# Revit family: SQN-HP
name_source: partatom
category: Mechanical Equipment
units: mm (PartAtom-declared; Revit-internal decimal feet)

## family parameters
Always vertical = Yes
Cut with Voids When Loaded = No
Part Type = Normal
Room Calculation Point = No
Round Connector Dimension = Use Diameter
Shared = No
Work Plane-Based = No

## types (13) — shared parameters
1.5 = 0' - 1 1/2"
HALF_F = 0' - 11 1/32"
HALF_G = 0' - 11 13/32"
Manufacturer = Loren Cook Company
Model = SQN-HP
ONE EIGTH = 0' - 0 1/8"
T_SQ = 1' - 0"
T_SQ_HALF = 0' - 6"
Type Comments = Centrifugal Square Inline High Pressure Belt Drive
URL = www.lorencook.com
ZERO = 0' - 0"

## per-type parameters (varying)
- 135_SQN-HP: A_SUB=1' - 6"; B_SUB=1' - 8 1/4"; B_SUB_MIN_.125=1' - 8 1/8"; C_SUB=1' - 10 1/4"; DEPTH=1' - 8 1/4"; D_PLUS_2=1' - 10 3/4"; D_SUB=1' - 8 3/4"; D_SUB_MINUS_.25=1' - 8 1/2"; D_SUB_TENTH=0' - 2 1/16"; E_SUB=1' - 0 1/2"; E_SUB_DIRECT=1' - 10 3/4"; FLANGE=0' - 1"; FOURTH_B=0' - 5 1/16"; F_SUB=1' - 1 1/8"; G_SUB=1' - 2 1/4"; HALFC-B=0' - 1"; HALF_2H+D=0' - 11 3/8"; HALF_B=0' - 10 1/8"; HALF_B-G=0' - 3"; HALF_D=0' - 10 3/8"; HALF_D-A=0' - 1 3/8"; HALF_D-F=0' - 3 13/16"; HALF_D_SUB=0' - 10 3/8"; HALF_D_SUB_MIN_.25=0' - 10 1/4"; HALF_MP=0' - 3 17/32"; INLET_RADIUS=0' - 5 3/16"; IN_RAD-D_SUB_TENTH=0' - 3 1/8"; IN_TENTH=0' - 3 1/8"; MOTOR_DEPTH=-0' - 11 7/8"; NEGHALFC-B=-0' - 1"; NEG_HALF2H+D=-0' - 11 3/8"; NEG_HALF_D=-0' - 10 3/8"; RAIL_SPACING=0' - 10 1/8"; SHAFT_RAD=0' - 1 1/32"; TENTHB+FOURTHB=-0' - 7 3/32"; TENTH_B=-0' - 2 1/32"
- 150_SQN-HP: A_SUB=1' - 8"; B_SUB=1' - 9 7/8"; B_SUB_MIN_.125=1' - 9 3/4"; C_SUB=1' - 11 7/8"; DEPTH=1' - 9 7/8"; D_PLUS_2=2' - 1"; D_SUB=1' - 11"; D_SUB_MINUS_.25=1' - 10 3/4"; D_SUB_TENTH=0' - 2 5/16"; E_SUB=1' - 0 3/4"; E_SUB_DIRECT=2' - 1"; FLANGE=0' - 1"; FOURTH_B=0' - 5 15/32"; F_SUB=1' - 4 1/8"; G_SUB=1' - 3 15/16"; HALFC-B=0' - 1"; HALF_2H+D=1' - 0 1/2"; HALF_B=0' - 10 15/16"; HALF_B-G=0' - 2 31/32"; HALF_D=0' - 11 1/2"; HALF_D-A=0' - 1 1/2"; HALF_D-F=0' - 3 7/16"; HALF_D_SUB=0' - 11 1/2"; HALF_D_SUB_MIN_.25=0' - 11 3/8"; HALF_MP=0' - 3 27/32"; INLET_RADIUS=0' - 5 3/4"; IN_RAD-D_SUB_TENTH=0' - 3 7/16"; IN_TENTH=0' - 3 7/16"; MOTOR_DEPTH=-1' - 0 11/16"; NEGHALFC-B=-0' - 1"; NEG_HALF2H+D=-1' - 0 1/2"; NEG_HALF_D=-0' - 11 1/2"; RAIL_SPACING=0' - 10 15/16"; SHAFT_RAD=0' - 1 1/16"; TENTHB+FOURTHB=-0' - 7 21/32"; TENTH_B=-0' - 2 3/16"
- 165_SQN-HP: A_SUB=1' - 10"; B_SUB=2' - 1"; B_SUB_MIN_.125=2' - 0 7/8"; C_SUB=2' - 3"; DEPTH=2' - 1"; D_PLUS_2=2' - 3 5/16"; D_SUB=2' - 1 5/16"; D_SUB_MINUS_.25=2' - 1 1/16"; D_SUB_TENTH=0' - 2 17/32"; E_SUB=1' - 2 3/4"; E_SUB_DIRECT=2' - 3 5/16"; FLANGE=0' - 1"; FOURTH_B=0' - 6 1/4"; F_SUB=1' - 6 1/8"; G_SUB=1' - 7 1/8"; HALFC-B=0' - 1"; HALF_2H+D=1' - 1 21/32"; HALF_B=1' - 0 1/2"; HALF_B-G=0' - 2 15/16"; HALF_D=1' - 0 21/32"; HALF_D-A=0' - 1 21/32"; HALF_D-F=0' - 3 19/32"; HALF_D_SUB=1' - 0 21/32"; HALF_D_SUB_MIN_.25=1' - 0 17/32"; HALF_MP=0' - 4 3/8"; INLET_RADIUS=0' - 6 11/32"; IN_RAD-D_SUB_TENTH=0' - 3 13/16"; IN_TENTH=0' - 3 13/16"; MOTOR_DEPTH=-1' - 2 1/4"; NEGHALFC-B=-0' - 1"; NEG_HALF2H+D=-1' - 1 21/32"; NEG_HALF_D=-1' - 0 21/32"; RAIL_SPACING=1' - 0 1/2"; SHAFT_RAD=0' - 1 7/32"; TENTHB+FOURTHB=-0' - 8 3/4"; TENTH_B=-0' - 2 1/2"
- 180_SQN-HP: A_SUB=2' - 0"; B_SUB=2' - 4"; B_SUB_MIN_.125=2' - 3 7/8"; C_SUB=2' - 6"; DEPTH=2' - 4"; D_PLUS_2=2' - 5 5/8"; D_SUB=2' - 3 5/8"; D_SUB_MINUS_.25=2' - 3 3/8"; D_SUB_TENTH=0' - 2 3/4"; E_SUB=1' - 2 3/4"; E_SUB_DIRECT=2' - 5 5/8"; FLANGE=0' - 1"; FOURTH_B=0' - 7"; F_SUB=1' - 8 1/8"; G_SUB=1' - 9"; HALFC-B=0' - 1"; HALF_2H+D=1' - 2 13/16"; HALF_B=1' - 2"; HALF_B-G=0' - 3 1/2"; HALF_D=1' - 1 13/16"; HALF_D-A=0' - 1 13/16"; HALF_D-F=0' - 3 3/4"; HALF_D_SUB=1' - 1 13/16"; HALF_D_SUB_MIN_.25=1' - 1 11/16"; HALF_MP=0' - 4 29/32"; INLET_RADIUS=0' - 6 29/32"; IN_RAD-D_SUB_TENTH=0' - 4 5/32"; IN_TENTH=0' - 4 5/32"; MOTOR_DEPTH=-1' - 3 3/4"; NEGHALFC-B=-0' - 1"; NEG_HALF2H+D=-1' - 2 13/16"; NEG_HALF_D=-1' - 1 13/16"; RAIL_SPACING=1' - 2"; SHAFT_RAD=0' - 1 7/32"; TENTHB+FOURTHB=-0' - 9 13/16"; TENTH_B=-0' - 2 13/16"
- 195_SQN-HP: A_SUB=2' - 2"; B_SUB=2' - 6 1/4"; B_SUB_MIN_.125=2' - 6 1/8"; C_SUB=2' - 8 1/4"; DEPTH=2' - 6 1/4"; D_PLUS_2=2' - 7 15/16"; D_SUB=2' - 5 15/16"; D_SUB_MINUS_.25=2' - 5 11/16"; D_SUB_TENTH=0' - 3"; E_SUB=1' - 3"; E_SUB_DIRECT=2' - 7 15/16"; FLANGE=0' - 1"; FOURTH_B=0' - 7 9/16"; F_SUB=1' - 10 1/8"; G_SUB=1' - 11 1/4"; HALFC-B=0' - 1"; HALF_2H+D=1' - 3 31/32"; HALF_B=1' - 3 1/8"; HALF_B-G=0' - 3 1/2"; HALF_D=1' - 2 31/32"; HALF_D-A=0' - 1 31/32"; HALF_D-F=0' - 3 29/32"; HALF_D_SUB=1' - 2 31/32"; HALF_D_SUB_MIN_.25=1' - 2 27/32"; HALF_MP=0' - 5 9/32"; INLET_RADIUS=0' - 7 1/2"; IN_RAD-D_SUB_TENTH=0' - 4 1/2"; IN_TENTH=0' - 4 1/2"; MOTOR_DEPTH=-1' - 4 7/8"; NEGHALFC-B=-0' - 1"; NEG_HALF2H+D=-1' - 3 31/32"; NEG_HALF_D=-1' - 2 31/32"; RAIL_SPACING=1' - 3 1/8"; SHAFT_RAD=0' - 1 1/4"; TENTHB+FOURTHB=-0' - 10 19/32"; TENTH_B=-0' - 3 1/32"
- 210_SQN-HP: A_SUB=2' - 4"; B_SUB=2' - 8"; B_SUB_MIN_.125=2' - 7 7/8"; C_SUB=2' - 11"; DEPTH=2' - 8"; D_PLUS_2=2' - 9 1/4"; D_SUB=2' - 7 1/4"; D_SUB_MINUS_.25=2' - 7"; D_SUB_TENTH=0' - 3 1/8"; E_SUB=1' - 3"; E_SUB_DIRECT=2' - 9 1/4"; FLANGE=0' - 2"; FOURTH_B=0' - 8"; F_SUB=2' - 0 1/8"; G_SUB=2' - 0 1/2"; HALFC-B=0' - 1 1/2"; HALF_2H+D=1' - 5 5/8"; HALF_B=1' - 4"; HALF_B-G=0' - 3 3/4"; HALF_D=1' - 3 5/8"; HALF_D-A=0' - 1 5/8"; HALF_D-F=0' - 3 9/16"; HALF_D_SUB=1' - 3 5/8"; HALF_D_SUB_MIN_.25=1' - 3 1/2"; HALF_MP=0' - 5 19/32"; INLET_RADIUS=0' - 7 13/16"; IN_RAD-D_SUB_TENTH=0' - 4 11/16"; IN_TENTH=0' - 4 11/16"; MOTOR_DEPTH=-1' - 5 3/4"; NEGHALFC-B=-0' - 1 1/2"; NEG_HALF2H+D=-1' - 5 5/8"; NEG_HALF_D=-1' - 3 5/8"; RAIL_SPACING=1' - 4"; SHAFT_RAD=0' - 1 1/4"; TENTHB+FOURTHB=-0' - 11 3/16"; TENTH_B=-0' - 3 3/16"
- 225_SQN-HP: A_SUB=2' - 6"; B_SUB=2' - 10 1/4"; B_SUB_MIN_.125=2' - 10 1/8"; C_SUB=3' - 1 1/4"; DEPTH=2' - 10 1/4"; D_PLUS_2=2' - 11 1/2"; D_SUB=2' - 9 1/2"; D_SUB_MINUS_.25=2' - 9 1/4"; D_SUB_TENTH=0' - 3 11/32"; E_SUB=1' - 3 1/4"; E_SUB_DIRECT=2' - 11 1/2"; FLANGE=0' - 2"; FOURTH_B=0' - 8 9/16"; F_SUB=2' - 2 1/8"; G_SUB=2' - 2 3/4"; HALFC-B=0' - 1 1/2"; HALF_2H+D=1' - 6 3/4"; HALF_B=1' - 5 1/8"; HALF_B-G=0' - 3 3/4"; HALF_D=1' - 4 3/4"; HALF_D-A=0' - 1 3/4"; HALF_D-F=0' - 3 11/16"; HALF_D_SUB=1' - 4 3/4"; HALF_D_SUB_MIN_.25=1' - 4 5/8"; HALF_MP=0' - 6"; INLET_RADIUS=0' - 8 3/8"; IN_RAD-D_SUB_TENTH=0' - 5 1/32"; IN_TENTH=0' - 5 1/32"; MOTOR_DEPTH=-1' - 6 7/8"; NEGHALFC-B=-0' - 1 1/2"; NEG_HALF2H+D=-1' - 6 3/4"; NEG_HALF_D=-1' - 4 3/4"; RAIL_SPACING=1' - 5 1/8"; SHAFT_RAD=0' - 1 9/32"; TENTHB+FOURTHB=-1' - 0"; TENTH_B=-0' - 3 7/16"
- 245_SQN-HP: A_SUB=2' - 9"; B_SUB=2' - 10"; B_SUB_MIN_.125=2' - 9 7/8"; C_SUB=3' - 2"; DEPTH=2' - 10"; D_PLUS_2=3' - 2"; D_SUB=3' - 0"; D_SUB_MINUS_.25=2' - 11 3/4"; D_SUB_TENTH=0' - 3 19/32"; E_SUB=1' - 5 1/4"; E_SUB_DIRECT=3' - 2"; FLANGE=0' - 2"; FOURTH_B=0' - 8 1/2"; F_SUB=2' - 5 1/8"; G_SUB=2' - 2 1/16"; HALFC-B=0' - 2"; HALF_2H+D=1' - 8"; HALF_B=1' - 5"; HALF_B-G=0' - 3 31/32"; HALF_D=1' - 6"; HALF_D-A=0' - 1 1/2"; HALF_D-F=0' - 3 7/16"; HALF_D_SUB=1' - 6"; HALF_D_SUB_MIN_.25=1' - 5 7/8"; HALF_MP=0' - 5 15/16"; INLET_RADIUS=0' - 9"; IN_RAD-D_SUB_TENTH=0' - 5 13/32"; IN_TENTH=0' - 5 13/32"; MOTOR_DEPTH=-1' - 6 3/4"; NEGHALFC-B=-0' - 2"; NEG_HALF2H+D=-1' - 8"; NEG_HALF_D=-1' - 6"; RAIL_SPACING=1' - 5"; SHAFT_RAD=0' - 1 7/16"; TENTHB+FOURTHB=-0' - 11 29/32"; TENTH_B=-0' - 3 13/32"
- 270_SQN-HP: A_SUB=3' - 0 7/16"; B_SUB=3' - 1 1/2"; B_SUB_MIN_.125=3' - 1 3/8"; C_SUB=3' - 5 1/2"; DEPTH=3' - 1 1/2"; D_PLUS_2=3' - 5 11/16"; D_SUB=3' - 3 11/16"; D_SUB_MINUS_.25=3' - 3 7/16"; D_SUB_TENTH=0' - 3 31/32"; E_SUB=1' - 5 1/4"; E_SUB_DIRECT=3' - 5 11/16"; FLANGE=0' - 2"; FOURTH_B=0' - 9 3/8"; F_SUB=2' - 8 1/2"; G_SUB=2' - 5 11/16"; HALFC-B=0' - 2"; HALF_2H+D=1' - 9 27/32"; HALF_B=1' - 6 3/4"; HALF_B-G=0' - 3 29/32"; HALF_D=1' - 7 27/32"; HALF_D-A=0' - 1 5/8"; HALF_D-F=0' - 3 19/32"; HALF_D_SUB=1' - 7 27/32"; HALF_D_SUB_MIN_.25=1' - 7 23/32"; HALF_MP=0' - 6 9/16"; INLET_RADIUS=0' - 9 15/16"; IN_RAD-D_SUB_TENTH=0' - 5 31/32"; IN_TENTH=0' - 5 31/32"; MOTOR_DEPTH=-1' - 8 1/2"; NEGHALFC-B=-0' - 2"; NEG_HALF2H+D=-1' - 9 27/32"; NEG_HALF_D=-1' - 7 27/32"; RAIL_SPACING=1' - 6 3/4"; SHAFT_RAD=0' - 1 7/16"; TENTHB+FOURTHB=-1' - 1 1/8"; TENTH_B=-0' - 3 3/4"
- 300_SQN-HP: A_SUB=3' - 4"; B_SUB=3' - 2"; B_SUB_MIN_.125=3' - 1 7/8"; C_SUB=3' - 6"; DEPTH=3' - 2"; D_PLUS_2=3' - 10"; D_SUB=3' - 8"; D_SUB_MINUS_.25=3' - 7 3/4"; D_SUB_TENTH=0' - 4 13/32"; E_SUB=1' - 5 1/4"; E_SUB_DIRECT=3' - 10"; FLANGE=0' - 2"; FOURTH_B=0' - 9 1/2"; F_SUB=3' - 0 1/8"; G_SUB=2' - 6 1/8"; HALFC-B=0' - 2"; HALF_2H+D=2' - 0"; HALF_B=1' - 7"; HALF_B-G=0' - 3 15/16"; HALF_D=1' - 10"; HALF_D-A=0' - 2"; HALF_D-F=0' - 3 15/16"; HALF_D_SUB=1' - 10"; HALF_D_SUB_MIN_.25=1' - 9 7/8"; HALF_MP=0' - 6 21/32"; INLET_RADIUS=0' - 11"; IN_RAD-D_SUB_TENTH=0' - 6 19/32"; IN_TENTH=0' - 6 19/32"; MOTOR_DEPTH=-1' - 8 3/4"; NEGHALFC-B=-0' - 2"; NEG_HALF2H+D=-2' - 0"; NEG_HALF_D=-1' - 10"; RAIL_SPACING=1' - 7"; SHAFT_RAD=0' - 1 7/16"; TENTHB+FOURTHB=-1' - 1 5/16"; TENTH_B=-0' - 3 13/16"
- 330_SQN-HP: A_SUB=3' - 8"; B_SUB=3' - 5 3/4"; B_SUB_MIN_.125=3' - 5 5/8"; C_SUB=3' - 9 3/4"; DEPTH=3' - 5 3/4"; D_PLUS_2=4' - 2 7/16"; D_SUB=4' - 0 7/16"; D_SUB_MINUS_.25=4' - 0 3/16"; D_SUB_TENTH=0' - 4 27/32"; E_SUB=1' - 5 1/4"; E_SUB_DIRECT=4' - 2 7/16"; FLANGE=0' - 2"; FOURTH_B=0' - 10 7/16"; F_SUB=3' - 4 1/8"; G_SUB=2' - 7 13/16"; HALFC-B=0' - 2"; HALF_2H+D=2' - 2 7/32"; HALF_B=1' - 8 7/8"; HALF_B-G=0' - 4 31/32"; HALF_D=2' - 0 7/32"; HALF_D-A=0' - 2 7/32"; HALF_D-F=0' - 4 5/32"; HALF_D_SUB=2' - 0 7/32"; HALF_D_SUB_MIN_.25=2' - 0 3/32"; HALF_MP=0' - 7 5/16"; INLET_RADIUS=1' - 0 1/8"; IN_RAD-D_SUB_TENTH=0' - 7 9/32"; IN_TENTH=0' - 7 9/32"; MOTOR_DEPTH=-1' - 10 5/8"; NEGHALFC-B=-0' - 2"; NEG_HALF2H+D=-2' - 2 7/32"; NEG_HALF_D=-2' - 0 7/32"; RAIL_SPACING=1' - 8 7/8"; SHAFT_RAD=0' - 1 7/16"; TENTHB+FOURTHB=-1' - 2 5/8"; TENTH_B=-0' - 4 3/16"
- 365_SQN-HP: A_SUB=3' - 10"; B_SUB=3' - 6"; B_SUB_MIN_.125=3' - 5 7/8"; C_SUB=3' - 10"; DEPTH=3' - 6"; D_PLUS_2=4' - 4"; D_SUB=4' - 2"; D_SUB_MINUS_.25=4' - 1 3/4"; D_SUB_TENTH=0' - 5"; E_SUB=1' - 5 1/4"; E_SUB_DIRECT=4' - 4"; FLANGE=0' - 2"; FOURTH_B=0' - 10 1/2"; F_SUB=3' - 6 1/16"; G_SUB=2' - 8 3/16"; HALFC-B=0' - 2"; HALF_2H+D=2' - 3"; HALF_B=1' - 9"; HALF_B-G=0' - 4 29/32"; HALF_D=2' - 1"; HALF_D-A=0' - 2"; HALF_D-F=0' - 3 31/32"; HALF_D_SUB=2' - 1"; HALF_D_SUB_MIN_.25=2' - 0 7/8"; HALF_MP=0' - 7 11/32"; INLET_RADIUS=1' - 0 1/2"; IN_RAD-D_SUB_TENTH=0' - 7 1/2"; IN_TENTH=0' - 7 1/2"; MOTOR_DEPTH=-1' - 10 3/4"; NEGHALFC-B=-0' - 2"; NEG_HALF2H+D=-2' - 3"; NEG_HALF_D=-2' - 1"; RAIL_SPACING=1' - 9"; SHAFT_RAD=0' - 1 7/16"; TENTHB+FOURTHB=-1' - 2 11/16"; TENTH_B=-0' - 4 3/16"
- 402_SQN-HP: A_SUB=4' - 2 3/4"; B_SUB=3' - 10 1/4"; B_SUB_MIN_.125=3' - 10 1/8"; C_SUB=4' - 2 1/4"; DEPTH=3' - 10 1/4"; D_PLUS_2=4' - 9 1/8"; D_SUB=4' - 7 1/8"; D_SUB_MINUS_.25=4' - 6 7/8"; D_SUB_TENTH=0' - 5 1/2"; E_SUB=1' - 5 1/4"; E_SUB_DIRECT=4' - 9 1/8"; FLANGE=0' - 2"; FOURTH_B=0' - 11 9/16"; F_SUB=3' - 10 15/16"; G_SUB=3' - 0 9/16"; HALFC-B=0' - 2"; HALF_2H+D=2' - 5 9/16"; HALF_B=1' - 11 1/8"; HALF_B-G=0' - 4 27/32"; HALF_D=2' - 3 9/16"; HALF_D-A=0' - 2 3/16"; HALF_D-F=0' - 4 3/32"; HALF_D_SUB=2' - 3 9/16"; HALF_D_SUB_MIN_.25=2' - 3 7/16"; HALF_MP=0' - 8 3/32"; INLET_RADIUS=1' - 1 25/32"; IN_RAD-D_SUB_TENTH=0' - 8 9/32"; IN_TENTH=0' - 8 9/32"; MOTOR_DEPTH=-2' - 0 7/8"; NEGHALFC-B=-0' - 2"; NEG_HALF2H+D=-2' - 5 9/16"; NEG_HALF_D=-2' - 3 9/16"; RAIL_SPACING=1' - 11 1/8"; SHAFT_RAD=0' - 1 7/16"; TENTHB+FOURTHB=-1' - 4 3/16"; TENTH_B=-0' - 4 5/8"

## geometry (parser evidence)
native form markers: Sweep x1
no freeform markers — native parametric forms only
